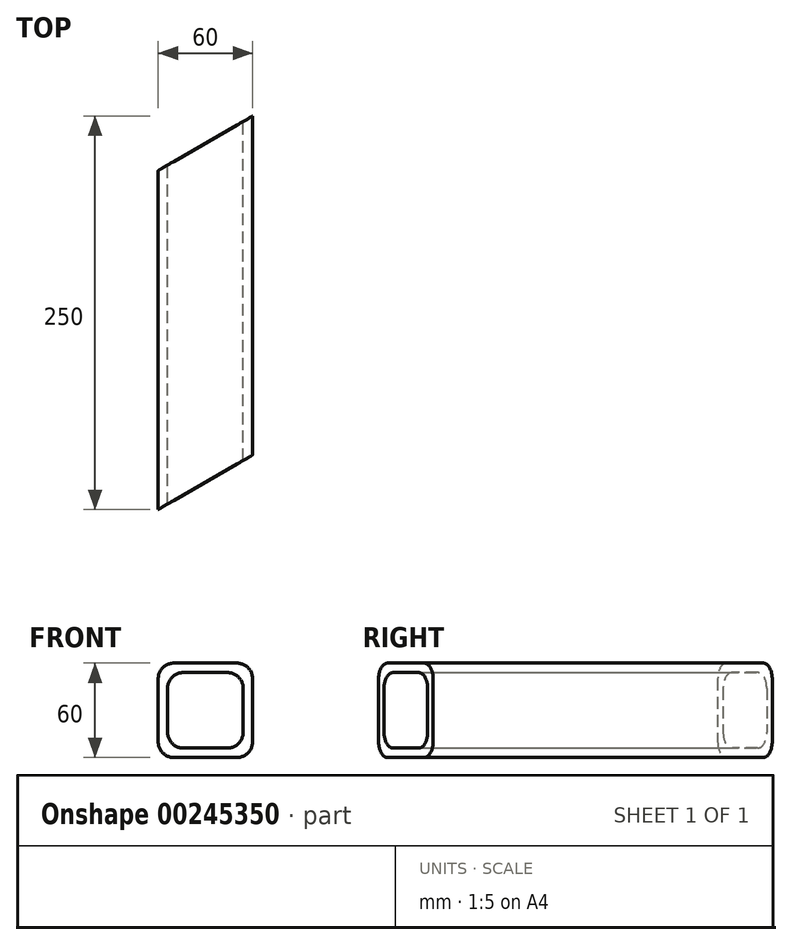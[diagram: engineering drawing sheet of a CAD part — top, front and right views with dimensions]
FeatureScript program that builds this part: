
annotation { "Feature Type Name" : "Feature", "Feature Type Description" : "" }
export const myFeature = defineFeature(function(context is Context, id is Id, definition is map)
    precondition{}
    {
        {
            var Q0;
            Q0=qCreatedBy(makeId("Front.planeOp"),FACE);
            var sketch = newSketch(context, id + "F0", { "sketchPlane" : qUnion([Q0])});
            skLineSegment(sketch, "E0.bottom", {"start": v(30, 30) * mm, "end": v(-30, 30) * mm});
            skLineSegment(sketch, "E0.top", {"start": v(30, -30) * mm, "end": v(-30, -30) * mm});
            skLineSegment(sketch, "E0.left", {"start": v(30, 30) * mm, "end": v(30, -30) * mm});
            skLineSegment(sketch, "E0.right", {"start": v(-30, 30) * mm, "end": v(-30, -30) * mm});
            skPoint(sketch, "E0.middle", {"position": v(0, 0) * mm});
            skSolve(sketch);
        }
        {
            var Q0;
            Q0=makeQuery(id+"F0.imprint","IMPRINT",FACE,{"disambiguationData":[TD([[makeQuery(id+"F0.imprint","IMPRINT",EDGE,{"derivedFrom":sQuery(id+"F0.wireOp",EDGE,"E0.bottom")}),1.0]])]});
            extrude(context, id + "F1", {"entities" : qUnion([Q0]), "depth" : 250 * mm});
        }
        {
            var Q0;
            Q0=makeQuery(id+"F1.opExtrude","CAP_FACE",FACE,{"disambiguationData":[OSD([sQuery(id+"F0.wireOp",EDGE,"E0.bottom"),sQuery(id+"F0.wireOp",EDGE,"E0.top"),sQuery(id+"F0.wireOp",EDGE,"E0.left"),sQuery(id+"F0.wireOp",EDGE,"E0.right")])],"isStart":false});
            var Q1;
            Q1=makeQuery(id+"F1.opExtrude","CAP_FACE",FACE,{"disambiguationData":[OSD([sQuery(id+"F0.wireOp",EDGE,"E0.bottom"),sQuery(id+"F0.wireOp",EDGE,"E0.top"),sQuery(id+"F0.wireOp",EDGE,"E0.left"),sQuery(id+"F0.wireOp",EDGE,"E0.right")])],"isStart":true});
            shell(context, id + "F2", {"entities" : qUnion([Q0, Q1]), "thickness" : 6 * mm});
        }
        {
            var Q0;
            Q0=makeQuery(id+"F1.opExtrude","SWEPT_EDGE",EDGE,{"disambiguationData":[OSD([sQuery(id+"F0.wireOp",EDGE,"E0.bottom"),sQuery(id+"F0.wireOp",EDGE,"E0.right")])]});
            var Q1;
            Q1=makeQuery(id+"F2.opShell","OFFSET_EDGE",EDGE,{"disambiguationData":[OSD([sQuery(id+"F0.wireOp",EDGE,"E0.top"),sQuery(id+"F0.wireOp",EDGE,"E0.right")])]});
            var Q2;
            Q2=makeQuery(id+"F1.opExtrude","SWEPT_EDGE",EDGE,{"disambiguationData":[OSD([sQuery(id+"F0.wireOp",EDGE,"E0.bottom"),sQuery(id+"F0.wireOp",EDGE,"E0.left")])]});
            var Q3;
            Q3=makeQuery(id+"F1.opExtrude","SWEPT_EDGE",EDGE,{"disambiguationData":[OSD([sQuery(id+"F0.wireOp",EDGE,"E0.top"),sQuery(id+"F0.wireOp",EDGE,"E0.left")])]});
            var Q4;
            Q4=makeQuery(id+"F2.opShell","OFFSET_EDGE",EDGE,{"disambiguationData":[OSD([sQuery(id+"F0.wireOp",EDGE,"E0.bottom"),sQuery(id+"F0.wireOp",EDGE,"E0.right")])]});
            var Q5;
            Q5=makeQuery(id+"F1.opExtrude","SWEPT_EDGE",EDGE,{"disambiguationData":[OSD([sQuery(id+"F0.wireOp",EDGE,"E0.top"),sQuery(id+"F0.wireOp",EDGE,"E0.right")])]});
            var Q6;
            Q6=makeQuery(id+"F2.opShell","OFFSET_EDGE",EDGE,{"disambiguationData":[OSD([sQuery(id+"F0.wireOp",EDGE,"E0.bottom"),sQuery(id+"F0.wireOp",EDGE,"E0.left")])]});
            var Q7;
            Q7=makeQuery(id+"F2.opShell","OFFSET_EDGE",EDGE,{"disambiguationData":[OSD([sQuery(id+"F0.wireOp",EDGE,"E0.top"),sQuery(id+"F0.wireOp",EDGE,"E0.left")])]});
            fillet(context, id + "F3", {"entities" : qUnion([Q0, Q1, Q2, Q3, Q4, Q5, Q6, Q7]), "radius" : 10 * mm, "tangentPropagation" : true, "allowEdgeOverflow" : false});
        }
        {
            var Q0;
            Q0=makeQuery(id+"F1.opExtrude","SWEPT_FACE",FACE,{"disambiguationData":[OSD([sQuery(id+"F0.wireOp",EDGE,"E0.bottom")])]});
            var sketch = newSketch(context, id + "F4", { "sketchPlane" : qUnion([Q0])});
            skLineSegment(sketch, "E1", {"start": v(40, -209.59) * mm, "end": v(-40, -255.77) * mm});
            skLineSegment(sketch, "E2", {"start": v(-40, -255.77) * mm, "end": v(40, -255.77) * mm});
            skLineSegment(sketch, "E3", {"start": v(40, -255.77) * mm, "end": v(40, -209.59) * mm});
            skSolve(sketch);
        }
        {
            var Q0;
            Q0 = qSketchRegion(id + "F4", true);
            extrude(context, id + "F5", {"entities" : qUnion([Q0]), "operationType" : NewBodyOperationType.REMOVE, "endBound" : BoundingType.THROUGH_ALL, "oppositeDirection" : true, "depth" : 25 * mm});
        }
        {
            var Q0;
            Q0=makeQuery(id+"F1.opExtrude","SWEPT_FACE",FACE,{"disambiguationData":[OSD([sQuery(id+"F0.wireOp",EDGE,"E0.bottom")])]});
            var sketch = newSketch(context, id + "F6", { "sketchPlane" : qUnion([Q0])});
            skLineSegment(sketch, "E4", {"start": v(-40, -40.41) * mm, "end": v(40, 5.77) * mm});
            skLineSegment(sketch, "E5", {"start": v(40, 5.77) * mm, "end": v(-40, 5.77) * mm});
            skLineSegment(sketch, "E6", {"start": v(-40, 5.77) * mm, "end": v(-40, -40.41) * mm});
            skSolve(sketch);
        }
        {
            var Q0;
            Q0 = qSketchRegion(id + "F6", true);
            extrude(context, id + "F7", {"entities" : qUnion([Q0]), "operationType" : NewBodyOperationType.REMOVE, "endBound" : BoundingType.THROUGH_ALL, "oppositeDirection" : true, "depth" : 25 * mm});
        }
    });
